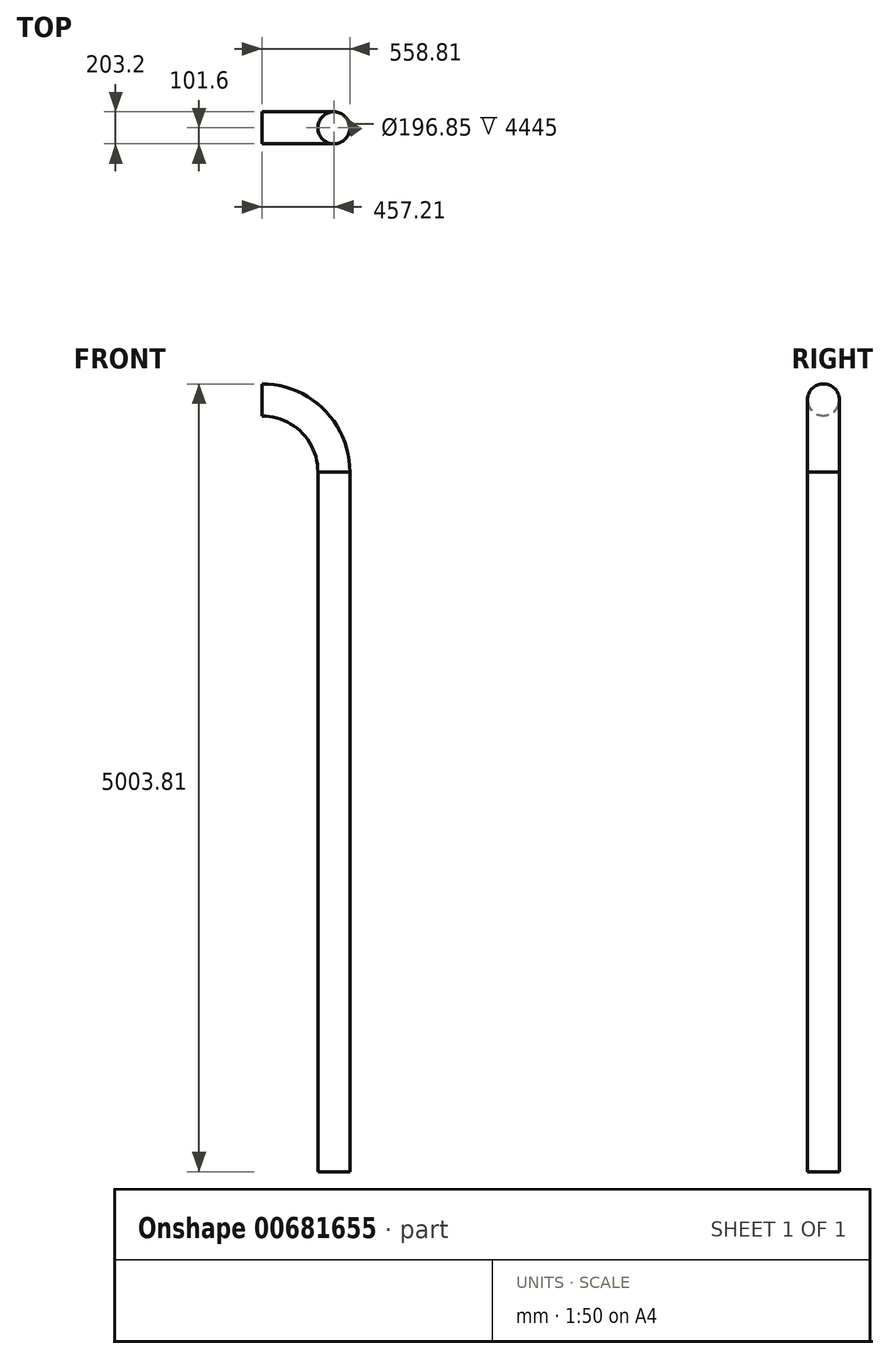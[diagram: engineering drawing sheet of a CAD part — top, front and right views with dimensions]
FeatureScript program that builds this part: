
annotation { "Feature Type Name" : "Feature", "Feature Type Description" : "" }
export const myFeature = defineFeature(function(context is Context, id is Id, definition is map)
    precondition{}
    {
        {
            var Q0;
            Q0=qCreatedBy(makeId("Front.planeOp"),FACE);
            var sketch = newSketch(context, id + "F0", { "sketchPlane" : qUnion([Q0])});
            skLineSegment(sketch, "E0", {"start": v(0, 0) * mm, "end": v(0, 3238.5) * mm, "construction": true});
            skLineSegment(sketch, "E1", {"start": v(0, 3238.5) * mm, "end": v(0, 4445) * mm, "construction": true});
            skLineSegment(sketch, "E2", {"start": v(0, 4445) * mm, "end": v(-457.2, 4445) * mm, "construction": true});
            skLineSegment(sketch, "E3", {"start": v(0, 3238.5) * mm, "end": v(-457.2, 3238.5) * mm, "construction": true});
            skLineSegment(sketch, "E4", {"start": v(0, 4445) * mm, "end": v(0, 4902.2) * mm, "construction": true});
            skLineSegment(sketch, "E5", {"start": v(0, 4902.2) * mm, "end": v(-457.2, 4902.2) * mm, "construction": true});
            skSolve(sketch);
        }
        {
            var Q0;
            Q0=qCreatedBy(makeId("Top.planeOp"),FACE);
            var sketch = newSketch(context, id + "F1", { "sketchPlane" : qUnion([Q0])});
            skCircle(sketch, "E6", {"center": v(0, 0) * mm, "radius": 98.43 * mm});
            skCircle(sketch, "E7", {"center": v(0, 0) * mm, "radius": 101.6 * mm});
            skSolve(sketch);
        }
        {
            var Q0;
            Q0=sQuery(id+"F0.wireOp",EDGE,"E3");
            cPlane(context, id + "F2", {"entities" : qUnion([Q0]), "cplaneType" : CPlaneType.LINE_ANGLE, "offset" : 25.4 * mm, "angle" : 90 * degree, "width" : 152.4 * mm, "height" : 152.4 * mm});
        }
        {
            var Q0;
            Q0=sQuery(id+"F0.wireOp",EDGE,"E2");
            cPlane(context, id + "F3", {"entities" : qUnion([Q0]), "cplaneType" : CPlaneType.LINE_ANGLE, "offset" : 25.4 * mm, "angle" : 90 * degree, "width" : 152.4 * mm, "height" : 152.4 * mm});
        }
        {
            var Q0;
            Q0=qCreatedBy(id+"F3.planeOp",FACE);
            var sketch = newSketch(context, id + "F4", { "sketchPlane" : qUnion([Q0])});
            skLineSegment(sketch, "E8", {"start": v(-457.21, 0) * mm, "end": v(-457.21, -203.2) * mm, "construction": true});
            skSolve(sketch);
        }
        {
            var Q0;
            Q0=qCreatedBy(id+"F2.planeOp",FACE);
            var sketch = newSketch(context, id + "F5", { "sketchPlane" : qUnion([Q0])});
            skCircle(sketch, "E9", {"center": v(0, 0) * mm, "radius": 101.6 * mm});
            skCircle(sketch, "E10", {"center": v(0, 0) * mm, "radius": 98.43 * mm});
            skSolve(sketch);
        }
        {
            var Q0;
            Q0=qCreatedBy(id+"F3.planeOp",FACE);
            var sketch = newSketch(context, id + "F6", { "sketchPlane" : qUnion([Q0])});
            skCircle(sketch, "E11", {"center": v(0, 0) * mm, "radius": 101.6 * mm});
            skCircle(sketch, "E12", {"center": v(0, 0) * mm, "radius": 98.43 * mm});
            skSolve(sketch);
        }
        {
            var Q0;
            Q0=makeQuery(id+"F6.imprint","IMPRINT",FACE,{"disambiguationData":[TD([[makeQuery(id+"F6.imprint","IMPRINT",EDGE,{"derivedFrom":sQuery(id+"F6.wireOp",EDGE,"E11")}),1.0]])]});
            var Q1;
            Q1=sQuery(id+"F4.wireOp",EDGE,"E8");
            revolve(context, id + "F7", {"surfaceOperationType" : NewSurfaceOperationType.NEW, "entities" : qUnion([Q0]), "axis" : qUnion([Q1]), "revolveType" : RevolveType.ONE_DIRECTION, "angle" : 90 * degree});
        }
        {
            var Q0;
            Q0=makeQuery(id+"F5.imprint","IMPRINT",FACE,{"disambiguationData":[TD([[makeQuery(id+"F5.imprint","IMPRINT",EDGE,{"derivedFrom":sQuery(id+"F5.wireOp",EDGE,"E9")}),1.0]])]});
            extrude(context, id + "F8", {"entities" : qUnion([Q0]), "depth" : 1206.5 * mm, "offsetDistance" : 25.4 * mm});
        }
        {
            var Q0;
            Q0=makeQuery(id+"F1.imprint","IMPRINT",FACE,{"disambiguationData":[TD([[makeQuery(id+"F1.imprint","IMPRINT",EDGE,{"derivedFrom":sQuery(id+"F1.wireOp",EDGE,"E6")}),-1.0]])]});
            extrude(context, id + "F9", {"entities" : qUnion([Q0]), "operationType" : NewBodyOperationType.ADD, "depth" : 3238.5 * mm, "offsetDistance" : 25.4 * mm});
        }
    });
